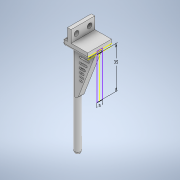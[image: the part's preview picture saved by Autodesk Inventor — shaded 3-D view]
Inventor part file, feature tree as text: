
AUTODESK INVENTOR PART (.ipt)
format: ipt  version: 2021 (Build 250183000, 183)  size: 510,976 bytes
history: native  units: mm
features: sketch x16, extrude x11, other x8, reference x8, fillet x5, projected_geometry x5, plane x4, split x2, delete_face x1, direct_edit x1, move_body x1
ambient origin geometry x8: Origin, YZ Plane, XZ Plane, XY Plane, X Axis, Y Axis, Z Axis, Center Point
bodies: Solid1 (feature_tree), Solid5 (feature_tree)
feature tree (62):
  extrude  "Extrusion1"  Depth=20.0mm
  extrude  "Extrusion3"  Depth=5.0mm
  extrude  "Extrusion4"  Depth=3.0mm
  extrude  "Extrusion5"  Depth=5.0mm TaperAngle=0.0deg
  extrude  "Extrusion6"  Depth=5.0mm TaperAngle=0.0deg
  plane  "Work Plane1"
  split  "Split1"
  extrude  "Extrusion7"  TaperAngle=0.0deg  [1 undecoded]
  extrude  "Extrusion8"  Depth=4.0mm TaperAngle=0.0deg
  fillet  "Fillet1"  Radius=2.5mm
  sketch  "Sketch9"  dims[d27=0.0mm d28=0.0mm d29=0.5mm d30=2.0mm d31=2.0mm d32=2.0mm]
  extrude  "Extrusion9"  TaperAngle=0.0deg  [1 undecoded]
  other  "Form4"
  plane  "Work Plane3"
  split  "Split3"
  delete_face  "Delete Face1"
  direct_edit  "Direct Edit1"
  fillet  "Fillet2"  Radius=2.0mm
  fillet  "Fillet3"  Radius=2.0mm
  fillet  "Fillet4"  Radius=2.0mm
  sketch  "Sketch11"  dims[d36=45.0mm d37=0.0mm d38=2.0mm d39=45.0mm d40=0.0mm]
  sketch  "Sketch2"  dims[d2=17.0mm d3=0.0mm d4=5.0mm]
  sketch  "Sketch12"
  plane  "Work Plane4"
  sketch  "Sketch13"
  plane  "Work Plane5"
  extrude  "Extrusion10"  Depth=45.0mm TaperAngle=0.0deg
  extrude  "Extrusion11"  Depth=2.0mm
  fillet  "Fillet5"  Radius=45.0mm
  extrude  "Extrusion12"  [1 undecoded]
  sketch  "Sketch1"  dims[d0=5.0mm d1=20.0mm]
  sketch  "Sketch3"  dims[d5=35.0mm d8=3.0mm]
  sketch  "Sketch4"  dims[d9=10.0mm d10=5.0mm d11=0.0mm]
  reference  "Reference1"
  reference  "Reference2"
  sketch  "Sketch5"  dims[d12=5.0mm d13=0.0mm d14=5.0mm d15=0.0mm]
  reference  "Reference3"
  reference  "Reference4"
  reference  "Reference5"
  reference  "Reference6"
  sketch  "Sketch6"  dims[d16=10.0mm d17=0.0mm d18=0.0mm]
  reference  "Reference7"
  reference  "Reference8"
  sketch  "Sketch7"  dims[d19=4.0mm d20=0.0mm d21=4.0mm d22=0.0mm d23=2.5mm]
  projected_geometry  "Projected Loop1"
  projected_geometry  "Projected Loop2"
  sketch  "Sketch8"  dims[d24=45.0mm d25=0.0mm d26=0.0mm]
  projected_geometry  "Projected Loop3"
  sketch  "Sketch10"  dims[d33=-40.0mm d34=45.0mm d35=0.0mm]
  projected_geometry  "Projected Loop4"
  sketch  "Sketch14"
  sketch  "Sketch15"
  projected_geometry  "Projected Loop5"
  sketch  "Sketch16"
  parser-record x3  (decoder bookkeeping rows leaked as tree rows — omitted from the tree; the rows remain in map.json)
  other  "whole_assembly.iam"
  other  "normal_finger:1"
  other  "reverse_finger:2"
  other  "normal_finger:2"
  move_body  "Move1"
note: 3 required parameter values undecoded (feature->parameter linkage not recoverable at this tier; creation-order binding heuristic only, values carry confidence <= 0.55)
note: 3 file-system paths scrubbed to <path> (originals preserved in map.json)
